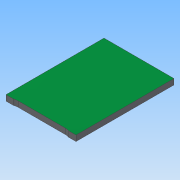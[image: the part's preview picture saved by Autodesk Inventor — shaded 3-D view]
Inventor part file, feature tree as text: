
AUTODESK INVENTOR PART (.ipt)
format: ipt  version: 2016 (Build 200138000, 138)  size: 371,200 bytes
history: native  units: mm
features: extrude x2, sketch x2, projected_geometry x1
ambient origin geometry x8: Origin, YZ Plane, XZ Plane, XY Plane, X Axis, Y Axis, Z Axis, Center Point
bodies: Body1 (feature_tree)
feature tree (5):
  extrude  "Extrusion4"  Depth=10.0mm
  extrude  "Extrusion5"  Depth=1.65mm
  sketch  "Sketch10"  dims[d7=14.0mm d8=10.0mm]
  sketch  "Sketch11"  dims[d9=0.1mm d11=1.65mm d12=2.0mm d13=0.8mm d14=0.0mm d15=100.0mm d17=1.0mm d18=10.0mm d20=10.0mm d22=0.7mm d23=0.45mm d24=1.15mm d25=0.3mm d26=50.0mm d28=1.0mm d29=10.0mm d31=10.0mm d33=0.3mm d34=0.7mm d35=60.0mm d37=1.1mm d38=10.0mm d40=10.0mm d42=1.6mm d43=1.45mm d45=40.0mm d47=1.15mm d48=20.0mm d50=1.15mm d53=1.15mm d54=1.15mm d56=2.63mm d58=2.78mm d59=8.7mm d60=50.0mm d62=1.0mm d63=10.0mm d65=10.0mm d67=0.05mm d68=0.0mm]
  projected_geometry  "Projected Loop1"
